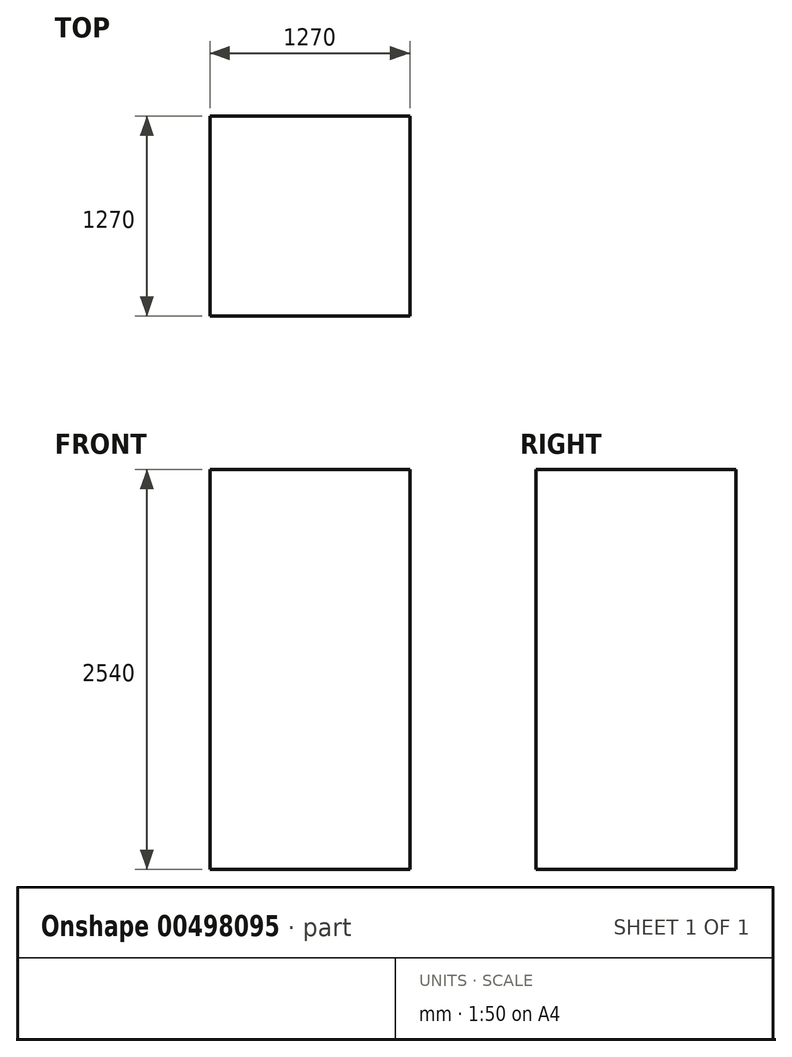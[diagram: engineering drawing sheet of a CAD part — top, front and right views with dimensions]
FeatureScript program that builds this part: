
annotation { "Feature Type Name" : "Feature", "Feature Type Description" : "" }
export const myFeature = defineFeature(function(context is Context, id is Id, definition is map)
    precondition{}
    {
        {
            var Q0;
            Q0=qCreatedBy(makeId("Top.planeOp"),FACE);
            var sketch = newSketch(context, id + "F0", { "sketchPlane" : qUnion([Q0])});
            skLineSegment(sketch, "E0.bottom", {"start": v(-635, 635) * mm, "end": v(635, 635) * mm});
            skLineSegment(sketch, "E0.top", {"start": v(-635, -635) * mm, "end": v(635, -635) * mm});
            skLineSegment(sketch, "E0.left", {"start": v(-635, 635) * mm, "end": v(-635, -635) * mm});
            skLineSegment(sketch, "E0.right", {"start": v(635, 635) * mm, "end": v(635, -635) * mm});
            skSolve(sketch);
        }
        {
            var Q0;
            Q0=makeQuery(id+"F0.imprint","IMPRINT",FACE,{"disambiguationData":[TD([[makeQuery(id+"F0.imprint","IMPRINT",EDGE,{"derivedFrom":sQuery(id+"F0.wireOp",EDGE,"E0.bottom")}),-1.0]])]});
            extrude(context, id + "F1", {"entities" : qUnion([Q0]), "depth" : 2540 * mm});
        }
    });
